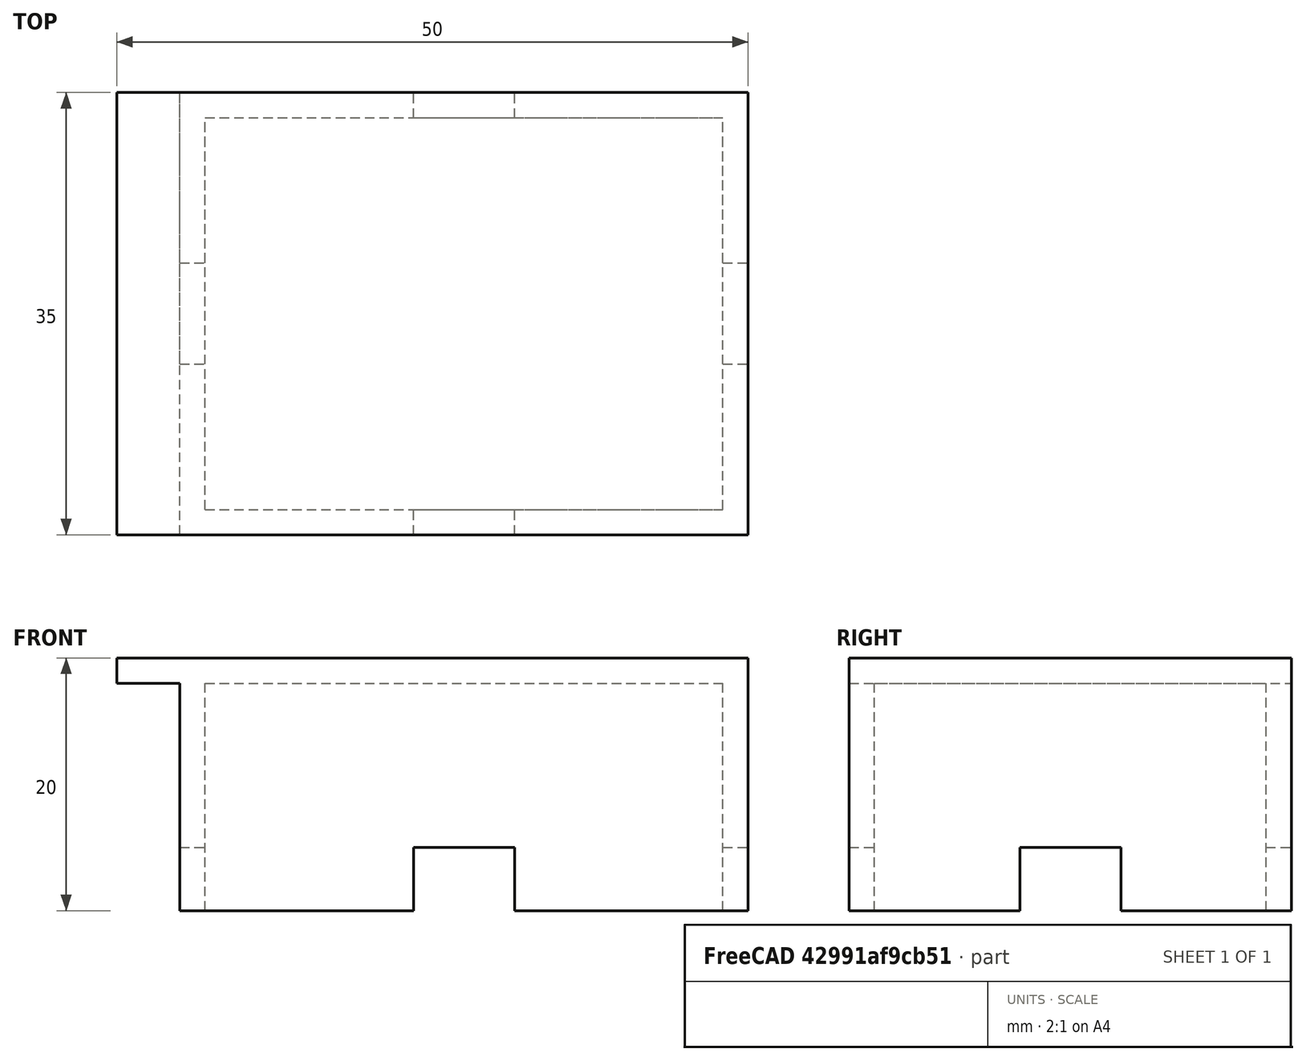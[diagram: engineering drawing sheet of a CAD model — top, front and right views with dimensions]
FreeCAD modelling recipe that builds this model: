
FCSTD DOCUMENT  (FreeCAD 0.16R6702 (Git))
Label: Tesela Buena
License: All rights reserved
LicenseURL: http://en.wikipedia.org/wiki/All_rights_reserved
objects: Part::Box×7, Part::Cut×6
note: 13 computed .brp shape members not serialized (recipe doc carries the construction recipe); baked Part::Feature solids carry a one-line shape summary decoded from their .brp

FEATURE [Part::Box] Box  label="Cubo"
  Height = 20
  Length = 50
  Width = 35
FEATURE [Part::Box] Box001  label="Cubo001"
  Height = 18
  Length = 5
  Width = 35
FEATURE [Part::Cut] Cut
  Base = -> Box
  Tool = -> Box001
FEATURE [Part::Box] Box002  label="Cubo002"
  Height = 18
  Length = 41
  Placement = pos=(7,2,0) rot=(0,0,1;0rad)
  Width = 31
FEATURE [Part::Cut] Cut001
  Base = -> Cut
  Tool = -> Box002
FEATURE [Part::Box] Box003  label="Cubo003"
  Height = 5
  Length = 8
  Placement = pos=(23.5,0,0) rot=(0,0,1;0rad)
  Width = 2
FEATURE [Part::Cut] Cut002
  Base = -> Cut001
  Tool = -> Box003
FEATURE [Part::Box] Box004  label="Cubo004"
  Height = 5
  Length = 8
  Placement = pos=(23.5,33,0) rot=(0,0,1;0rad)
  Width = 2
FEATURE [Part::Cut] Cut003
  Base = -> Cut002
  Tool = -> Box004
FEATURE [Part::Box] Box005  label="Cubo005"
  Height = 5
  Length = 2
  Placement = pos=(5,13.5,0) rot=(0,0,1;0rad)
  Width = 8
FEATURE [Part::Cut] Cut004
  Base = -> Cut003
  Tool = -> Box005
FEATURE [Part::Box] Box006  label="Cubo006"
  Height = 5
  Length = 2
  Placement = pos=(48,13.5,0) rot=(0,0,1;0rad)
  Width = 8
FEATURE [Part::Cut] Cut005
  Base = -> Cut004
  Tool = -> Box006
